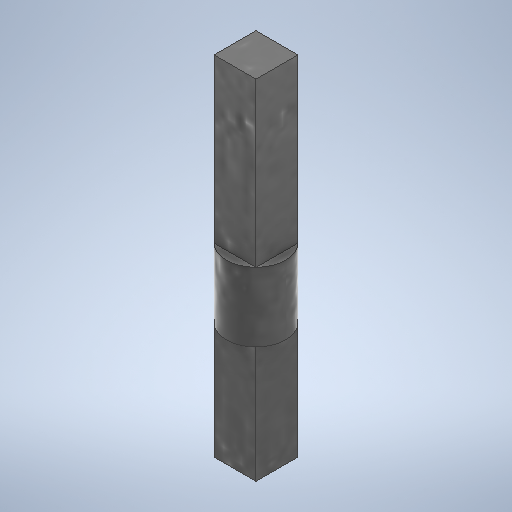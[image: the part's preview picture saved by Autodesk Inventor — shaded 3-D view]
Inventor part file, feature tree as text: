
AUTODESK INVENTOR PART (.ipt)
format: ipt  version: 2025.2 (Build 292293000, 293)  size: 272,384 bytes
history: native  units: mm
features: extrude x3, sketch x3
ambient origin geometry x8: Origin, YZ Plane, XZ Plane, XY Plane, X Axis, Y Axis, Z Axis, Center Point
bodies: Solid1 (feature_tree)
feature tree (6):
  extrude  "Extrusion1"  Depth=9.3mm TaperAngle=0.0deg
  extrude  "Extrusion2"  Depth=15.7mm TaperAngle=0.0deg
  extrude  "Extrusion3"  [1 undecoded]
  sketch  "Sketch1"  dims[d0=8.0mm d1=9.3mm d2=0.0mm]
  sketch  "Sketch2"  dims[d3=22.0mm d4=0.0mm d5=15.7mm d6=0.0mm]
  sketch  "Sketch3"
note: 1 required parameter value undecoded (feature->parameter linkage not recoverable at this tier; creation-order binding heuristic only, values carry confidence <= 0.55)
